# Revit family: M_Wood Timber Column
name_source: partatom
category: Columns
revit_build: Autodesk Revit Architecture 2012 (Build: 20110210_1515)
units: mm (PartAtom-declared; Revit-internal decimal feet)

## types (7) — shared parameters
Material = Wood - Dimensional Lumber

## per-type parameters (varying)
| type | Depth | Width |
| 140 x 191mm | 191 mm  [stored 0.62664 ft] | 140 mm  [stored 0.459318 ft] |
| 191 x 191mm | 191 mm  [stored 0.62664 ft] | 191 mm  [stored 0.62664 ft] |
| 140 x 140mm | 140 mm  [stored 0.459318 ft] | 140 mm  [stored 0.459318 ft] |
| 191 x 241mm | 241 mm | 191 mm  [stored 0.62664 ft] |
| 114 x 114mm | 114 mm | 114 mm |
| 140 x 241mm | 241 mm | 140 mm  [stored 0.459318 ft] |
| 191 x 292mm | 292 mm | 191 mm  [stored 0.62664 ft] |

note: [stored X ft] marks values corroborated as IEEE doubles in the binary element streams (Revit-internal decimal feet)

## geometry (parser evidence)
native form markers: Sweep x1
no freeform markers — native parametric forms only
